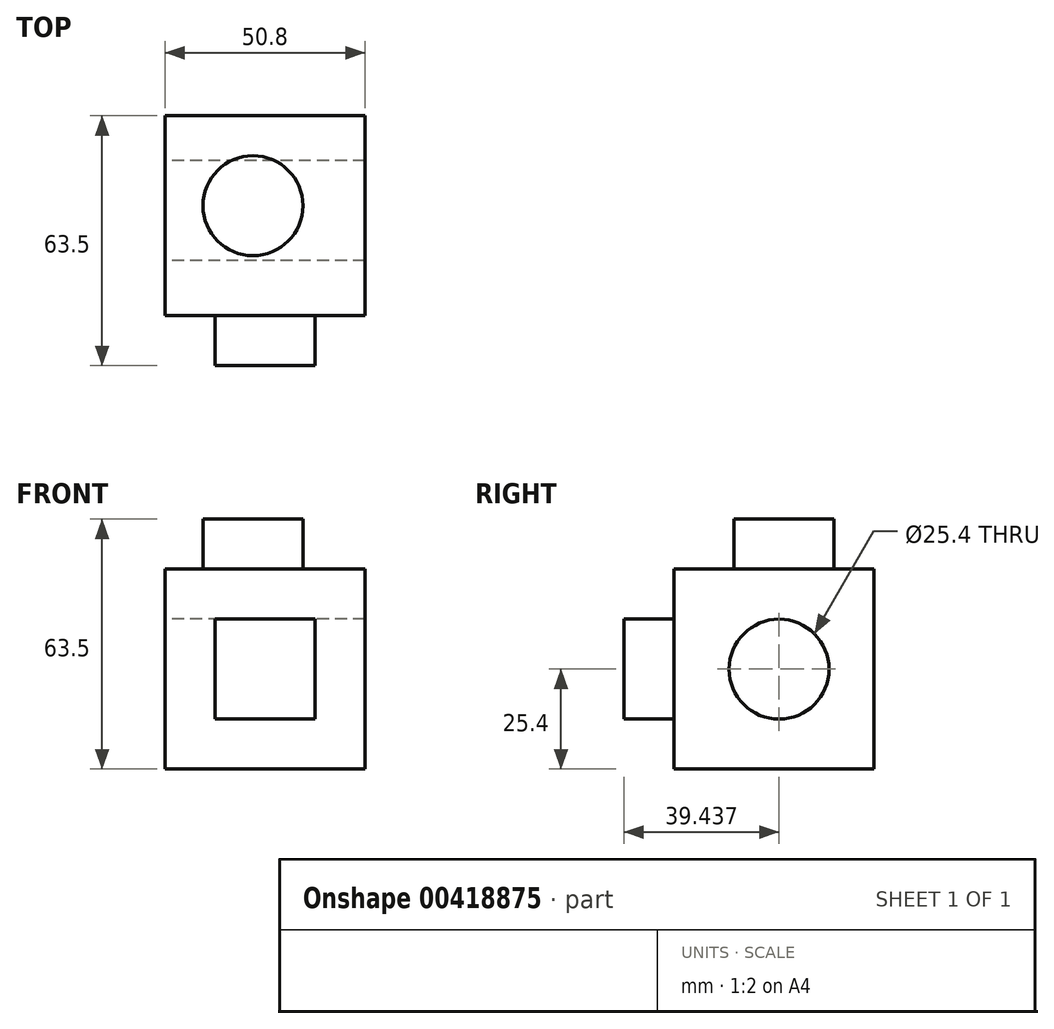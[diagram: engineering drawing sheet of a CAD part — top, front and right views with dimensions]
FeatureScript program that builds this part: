
annotation { "Feature Type Name" : "Feature", "Feature Type Description" : "" }
export const myFeature = defineFeature(function(context is Context, id is Id, definition is map)
    precondition{}
    {
        {
            var Q0;
            Q0=qCreatedBy(makeId("Front.planeOp"),FACE);
            var sketch = newSketch(context, id + "F0", { "sketchPlane" : qUnion([Q0])});
            skLineSegment(sketch, "E0.bottom", {"start": v(0, 0) * mm, "end": v(-50.8, 0) * mm});
            skLineSegment(sketch, "E0.top", {"start": v(0, 50.8) * mm, "end": v(-50.8, 50.8) * mm});
            skLineSegment(sketch, "E0.left", {"start": v(0, 0) * mm, "end": v(0, 50.8) * mm});
            skLineSegment(sketch, "E0.right", {"start": v(-50.8, 0) * mm, "end": v(-50.8, 50.8) * mm});
            skSolve(sketch);
        }
        {
            var Q0;
            Q0 = qSketchRegion(id + "F0", true);
            extrude(context, id + "F1", {"entities" : qUnion([Q0]), "depth" : 50.8 * mm});
        }
        {
            var Q0;
            Q0=makeQuery(id+"F1.opExtrude","CAP_FACE",FACE,{"disambiguationData":[OSD([sQuery(id+"F0.wireOp",EDGE,"E0.bottom"),sQuery(id+"F0.wireOp",EDGE,"E0.top"),sQuery(id+"F0.wireOp",EDGE,"E0.left"),sQuery(id+"F0.wireOp",EDGE,"E0.right")])],"isStart":false});
            var sketch = newSketch(context, id + "F2", { "sketchPlane" : qUnion([Q0])});
            skLineSegment(sketch, "E1.bottom", {"start": v(-38.1, 38.1) * mm, "end": v(-12.7, 38.1) * mm});
            skLineSegment(sketch, "E1.top", {"start": v(-38.1, 12.7) * mm, "end": v(-12.7, 12.7) * mm});
            skLineSegment(sketch, "E1.left", {"start": v(-38.1, 38.1) * mm, "end": v(-38.1, 12.7) * mm});
            skLineSegment(sketch, "E1.right", {"start": v(-12.7, 38.1) * mm, "end": v(-12.7, 12.7) * mm});
            skSolve(sketch);
        }
        {
            var Q0;
            Q0 = qSketchRegion(id + "F2", true);
            extrude(context, id + "F3", {"entities" : qUnion([Q0]), "operationType" : NewBodyOperationType.ADD, "depth" : 12.7 * mm});
        }
        {
            var Q0;
            Q0=makeQuery(id+"F1.opExtrude","SWEPT_FACE",FACE,{"disambiguationData":[OSD([sQuery(id+"F0.wireOp",EDGE,"E0.right")])]});
            var sketch = newSketch(context, id + "F4", { "sketchPlane" : qUnion([Q0])});
            skCircle(sketch, "E2", {"center": v(24.06, 25.4) * mm, "radius": 12.7 * mm});
            skSolve(sketch);
        }
        {
            var Q0;
            Q0 = qSketchRegion(id + "F4", true);
            extrude(context, id + "F5", {"entities" : qUnion([Q0]), "operationType" : NewBodyOperationType.REMOVE, "oppositeDirection" : true, "depth" : 50.8 * mm});
        }
        {
            var Q0;
            Q0=makeQuery(id+"F1.opExtrude","SWEPT_FACE",FACE,{"disambiguationData":[OSD([sQuery(id+"F0.wireOp",EDGE,"E0.top")])]});
            var sketch = newSketch(context, id + "F6", { "sketchPlane" : qUnion([Q0])});
            skCircle(sketch, "E3", {"center": v(-28.47, -22.86) * mm, "radius": 12.7 * mm});
            skSolve(sketch);
        }
        {
            var Q0;
            Q0=makeQuery(id+"F6.imprint","IMPRINT",FACE,{"disambiguationData":[TD([[makeQuery(id+"F6.imprint","IMPRINT",EDGE,{"derivedFrom":sQuery(id+"F6.wireOp",EDGE,"E3")}),1.0]])]});
            extrude(context, id + "F7", {"entities" : qUnion([Q0]), "operationType" : NewBodyOperationType.ADD, "depth" : 12.7 * mm});
        }
    });
